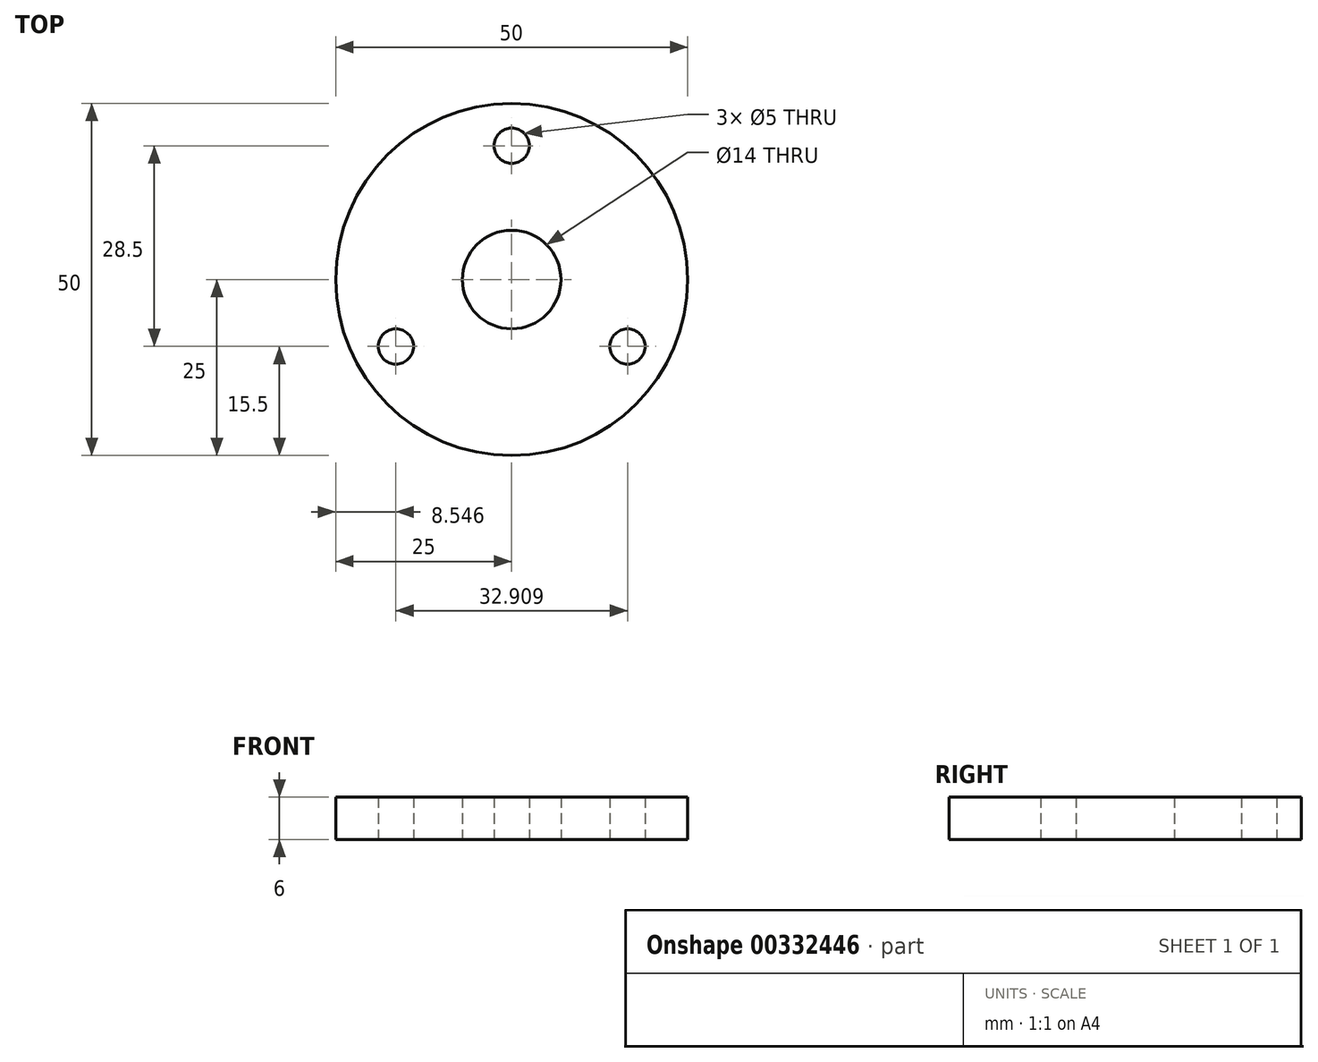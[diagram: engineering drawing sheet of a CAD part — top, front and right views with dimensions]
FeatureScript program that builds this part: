
annotation { "Feature Type Name" : "Feature", "Feature Type Description" : "" }
export const myFeature = defineFeature(function(context is Context, id is Id, definition is map)
    precondition{}
    {
        {
            var Q0;
            Q0=qCreatedBy(makeId("Top.planeOp"),FACE);
            var sketch = newSketch(context, id + "F0", { "sketchPlane" : qUnion([Q0])});
            skCircle(sketch, "E0", {"center": v(0, 0) * mm, "radius": 7 * mm});
            skCircle(sketch, "E1", {"center": v(0, 0) * mm, "radius": 25 * mm});
            skPoint(sketch, "E2", {"position": v(0, 19) * mm});
            skPoint(sketch, "E3", {"position": v(-16.45, -9.5) * mm});
            skPoint(sketch, "E4", {"position": v(16.45, -9.5) * mm});
            skCircle(sketch, "E5", {"center": v(0, 19) * mm, "radius": 2.5 * mm});
            skCircle(sketch, "E6", {"center": v(-16.45, -9.5) * mm, "radius": 2.5 * mm});
            skCircle(sketch, "E7", {"center": v(16.45, -9.5) * mm, "radius": 2.5 * mm});
            skSolve(sketch);
        }
        {
            var Q0;
            Q0 = qSketchRegion(id + "F0", true);
            extrude(context, id + "F1", {"entities" : qUnion([Q0]), "depth" : 6 * mm});
        }
    });
